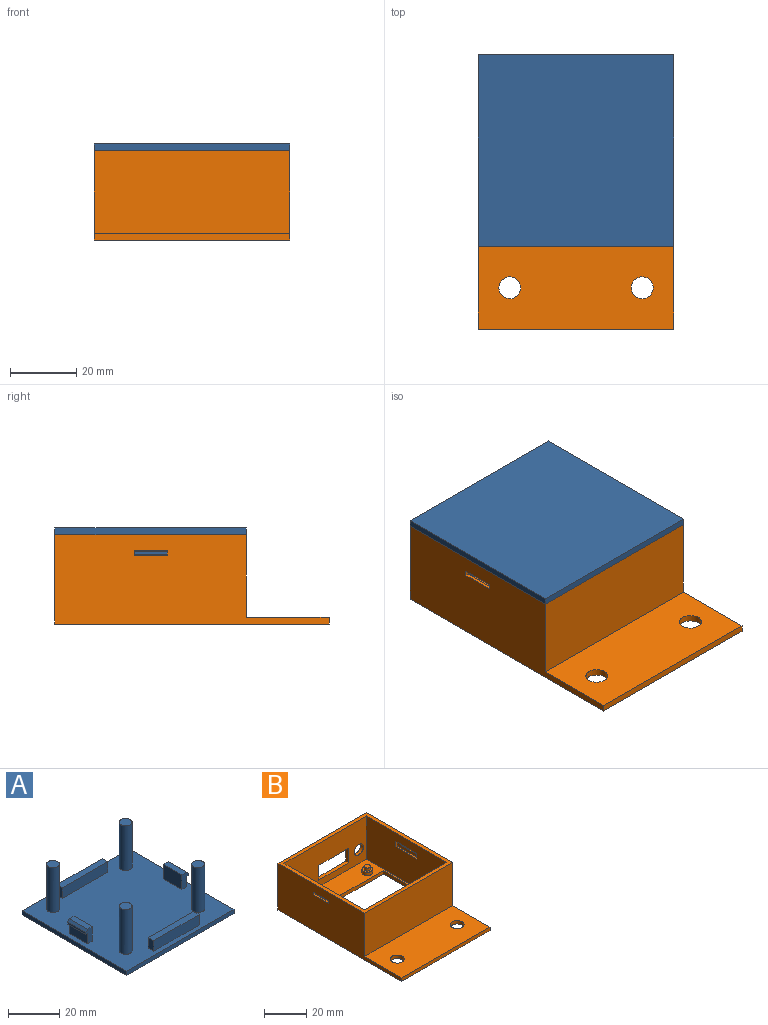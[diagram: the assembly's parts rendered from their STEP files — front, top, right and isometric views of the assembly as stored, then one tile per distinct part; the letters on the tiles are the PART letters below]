
ASSEMBLY  parts=2 mates=1
PART A: 40 faces, bbox 59x57.8x23.3 mm
  f0: plane 59x57.8mm, normal (0,0,1), area 3131.7mm2, adj f1,f2,f3,f4,f7,f9,f11,f13
  f1: plane 59x2mm, normal (0,1,0), area 118mm2, adj f0,f2,f4,f5
  f2: plane 57.8x2mm, normal (-1,0,0), area 115.6mm2, adj f0,f1,f3,f5
  f3: plane 59x2mm, normal (0,-1,0), area 118mm2, adj f0,f2,f4,f5
  f4: plane 57.8x2mm, normal (1,0,0), area 115.6mm2, adj f0,f1,f3,f5
  f5: plane 59x57.8mm, normal (0,0,-1), area 3410.2mm2, adj f1,f2,f3,f4
  f6: plane 5x5mm, normal (0,0,1), area 19.6mm2, adj f7
  f7: cylinder r=2.5mm len=21.3mm, axis (0,0,-1), area 334.6mm2, adj f0,f6
  f8: plane 5x5mm, normal (0,0,1), area 19.6mm2, adj f9
  f9: cylinder r=2.5mm len=21.3mm, axis (0,0,-1), area 334.6mm2, adj f0,f8
  f10: plane 5x5mm, normal (0,0,1), area 19.6mm2, adj f11
  f11: cylinder r=2.5mm len=21.3mm, axis (0,0,-1), area 334.6mm2, adj f0,f10
  f12: plane 5x5mm, normal (0,0,1), area 19.6mm2, adj f13
  f13: cylinder r=2.5mm len=21.3mm, axis (0,0,-1), area 334.6mm2, adj f0,f12
  f14: plane 10x5mm, normal (1,0,0), area 50mm2, adj f0,f15,f20,f21
  f15: plane 10x1mm, normal (0,0,-1), area 10mm2, adj f14,f16,f20,f21
  f16: plane 10x1mm, normal (1,0,0), area 10mm2, adj f15,f17,f20,f21
  f17: plane 10x1mm, normal (0.71,0,0.71), area 14.1mm2, adj f16,f18,f20,f21
  f18: plane 10x2.5mm, normal (0,0,1), area 25mm2, adj f17,f19,f20,f21
  f19: plane 10x7mm, normal (-1,0,0), area 70mm2, adj f0,f18,f20,f21
  f20: plane 7x3.5mm, normal (0,-1,0), area 19mm2, adj f0,f14,f15,f16,f17,f18,f19
  f21: plane 7x3.5mm, normal (0,1,0), area 19mm2, adj f0,f14,f15,f16,f17,f18,f19
  f22: plane 10x5mm, normal (-1,0,0), area 50mm2, adj f0,f27,f28,f29
  f23: plane 10x7mm, normal (1,0,0), area 70mm2, adj f0,f24,f28,f29
  f24: plane 10x2.5mm, normal (0,0,1), area 25mm2, adj f23,f25,f28,f29
  f25: plane 10x1mm, normal (-0.71,0,0.71), area 14.1mm2, adj f24,f26,f28,f29
  f26: plane 10x1mm, normal (-1,0,0), area 10mm2, adj f25,f27,f28,f29
  f27: plane 10x1mm, normal (0,0,-1), area 10mm2, adj f22,f26,f28,f29
  f28: plane 7x3.5mm, normal (0,-1,0), area 19mm2, adj f0,f22,f23,f24,f25,f26,f27
  f29: plane 7x3.5mm, normal (0,1,0), area 19mm2, adj f0,f22,f23,f24,f25,f26,f27
  f30: plane 25x5mm, normal (0,1,0), area 125mm2, adj f0,f31,f33,f34
  f31: plane 5x3mm, normal (-1,0,0), area 15mm2, adj f0,f30,f32,f34
  f32: plane 25x5mm, normal (0,-1,0), area 125mm2, adj f0,f31,f33,f34
  f33: plane 5x3mm, normal (1,0,0), area 15mm2, adj f0,f30,f32,f34
  f34: plane 25x3mm, normal (0,0,1), area 75mm2, adj f30,f31,f32,f33
  f35: plane 25x5mm, normal (0,1,0), area 125mm2, adj f0,f36,f38,f39
  f36: plane 5x3mm, normal (-1,0,0), area 15mm2, adj f0,f35,f37,f39
  f37: plane 25x5mm, normal (0,-1,0), area 125mm2, adj f0,f36,f38,f39
  f38: plane 5x3mm, normal (1,0,0), area 15mm2, adj f0,f35,f37,f39
  f39: plane 25x3mm, normal (0,0,1), area 75mm2, adj f35,f36,f37,f38
PART B: 56 faces, bbox 59x82.8x27 mm
  f0: plane 82.8x27mm, normal (-1,0,0), area 1595.6mm2, adj f4,f6,f10,f12,f30,f32,f38,f51
  f1: plane 82.8x27mm, normal (1,0,0), area 1595.6mm2, adj f4,f6,f10,f12,f30,f32,f45,f48
  f2: plane 53.8x25mm, normal (-1,0,0), area 1300.2mm2, adj f5,f13,f31,f32,f43,f45,f46,f47
  f3: plane 53.8x25mm, normal (1,0,0), area 1300.2mm2, adj f5,f13,f31,f32,f38,f40,f41,f42
  f4: plane 59x27mm, normal (0,1,0), area 1394.7mm2, adj f0,f1,f12,f32,f33,f34,f35,f36
  f5: plane 55x25mm, normal (0,-1,0), area 1176.7mm2, adj f2,f3,f13,f32,f33,f34,f35,f36
  f6: plane 59x25mm, normal (0,0,1), area 1406.6mm2, adj f0,f1,f10,f30,f54,f55
  f7: plane 33.84x2mm, normal (1,0,0), area 67.7mm2, adj f8,f11,f12,f13
  f8: plane 52.98x2mm, normal (0,-1,0), area 106mm2, adj f7,f9,f12,f13
  f9: plane 33.84x2mm, normal (-1,0,0), area 67.7mm2, adj f8,f11,f12,f13
  f10: plane 59x2mm, normal (0,-1,0), area 118mm2, adj f0,f1,f6,f12
  f11: plane 52.98x2mm, normal (0,1,0), area 106mm2, adj f7,f9,f12,f13
  f12: plane 82.8x59mm, normal (0,0,-1), area 3024.1mm2, adj f0,f1,f4,f7,f8,f9,f10,f11
  f13: plane 55x53.8mm, normal (0,0,1), area 1101.9mm2, adj f2,f3,f5,f7,f8,f9,f11,f14
  f14: cylinder r=2.5mm len=5mm, axis (0,0,-1), area 31.4mm2, adj f13,f15
  f15: plane 5x5mm, normal (0,0,1), area 12.6mm2, adj f14,f28
  f16: cylinder r=2.5mm len=5mm, axis (0,0,-1), area 31.4mm2, adj f13,f17
  f17: plane 5x5mm, normal (0,0,1), area 12.6mm2, adj f16,f26
  f18: cylinder r=2mm len=4mm, axis (0,0,-1), area 25.1mm2, adj f13,f19
  f19: plane 4x4mm, normal (0,0,1), area 5.5mm2, adj f18,f22
  f20: cylinder r=2mm len=4mm, axis (0,0,-1), area 25.1mm2, adj f13,f21
  f21: plane 4x4mm, normal (0,0,1), area 5.5mm2, adj f20,f24
  f22: cylinder r=1.5mm len=3mm, axis (0,0,-1), area 16mm2, adj f19,f23
  f23: plane 3x3mm, normal (0,0,1), area 7.1mm2, adj f22
  f24: cylinder r=1.5mm len=3mm, axis (0,0,-1), area 16mm2, adj f21,f25
  f25: plane 3x3mm, normal (0,0,1), area 7.1mm2, adj f24
  f26: cylinder r=1.5mm len=3mm, axis (0,0,-1), area 16mm2, adj f17,f27
  f27: plane 3x3mm, normal (0,0,1), area 7.1mm2, adj f26
  f28: cylinder r=1.5mm len=3mm, axis (0,0,-1), area 16mm2, adj f15,f29
  f29: plane 3x3mm, normal (0,0,1), area 7.1mm2, adj f28
  f30: plane 59x25mm, normal (0,-1,0), area 1475mm2, adj f0,f1,f6,f32
  f31: plane 55x25mm, normal (0,1,0), area 1375mm2, adj f2,f3,f13,f32
  f32: plane 59x57.8mm, normal (0,0,1), area 451.2mm2, adj f0,f1,f2,f3,f4,f5,f30,f31
  f33: cylinder r=3mm len=6mm, axis (0,1,0), area 37.7mm2, adj f4,f5
  f34: plane 20x2mm, normal (0,0,1), area 40mm2, adj f4,f5,f35,f37
  f35: plane 8.5x2mm, normal (1,0,0), area 17mm2, adj f4,f5,f34,f36
  f36: plane 20x2mm, normal (0,0,-1), area 40mm2, adj f4,f5,f35,f37
  f37: plane 8.5x2mm, normal (-1,0,0), area 17mm2, adj f4,f5,f34,f36
  f38: plane 14x2mm, normal (0,0,-1), area 23.8mm2, adj f0,f3,f39,f41,f42,f52,f53
  f39: plane 14x3.2mm, normal (1,0,0), area 29.8mm2, adj f38,f40,f41,f42,f51,f52,f53
  f40: plane 14x0.95mm, normal (0,0,1), area 13.3mm2, adj f3,f39,f41,f42
  f41: plane 3.2x0.95mm, normal (0,1,0), area 3mm2, adj f3,f38,f39,f40
  f42: plane 3.2x0.95mm, normal (0,-1,0), area 3mm2, adj f3,f38,f39,f40
  f43: plane 14x0.95mm, normal (0,0,1), area 13.3mm2, adj f2,f44,f46,f47
  f44: plane 14x3.2mm, normal (-1,0,0), area 29.8mm2, adj f43,f45,f46,f47,f48,f49,f50
  f45: plane 14x2mm, normal (0,0,-1), area 23.8mm2, adj f1,f2,f44,f46,f47,f49,f50
  f46: plane 3.2x0.95mm, normal (0,1,0), area 3mm2, adj f2,f43,f44,f45
  f47: plane 3.2x0.95mm, normal (0,-1,0), area 3mm2, adj f2,f43,f44,f45
  f48: plane 10x1.05mm, normal (0,0,1), area 10.5mm2, adj f1,f44,f49,f50
  f49: plane 1.5x1.05mm, normal (0,-1,0), area 1.6mm2, adj f1,f44,f45,f48
  f50: plane 1.5x1.05mm, normal (0,1,0), area 1.6mm2, adj f1,f44,f45,f48
  f51: plane 10x1.05mm, normal (0,0,1), area 10.5mm2, adj f0,f39,f52,f53
  f52: plane 1.5x1.05mm, normal (0,-1,0), area 1.6mm2, adj f0,f38,f39,f51
  f53: plane 1.5x1.05mm, normal (0,1,0), area 1.6mm2, adj f0,f38,f39,f51
  f54: cylinder r=3.3mm len=6.6mm, axis (0,0,1), area 41.5mm2, adj f6,f12
  f55: cylinder r=3.3mm len=6.6mm, axis (0,0,1), area 41.5mm2, adj f6,f12
PLACE A rot(axis=(1,0,0),180deg) t=(-30.37,7.28,22.47)mm
PLACE B t=(-10.44,-7.11,-2.53)mm
MATE fastened A.f0 <-> B.f32  axis (0,0,-1) through (21.13,-20.25,22.47)mm
